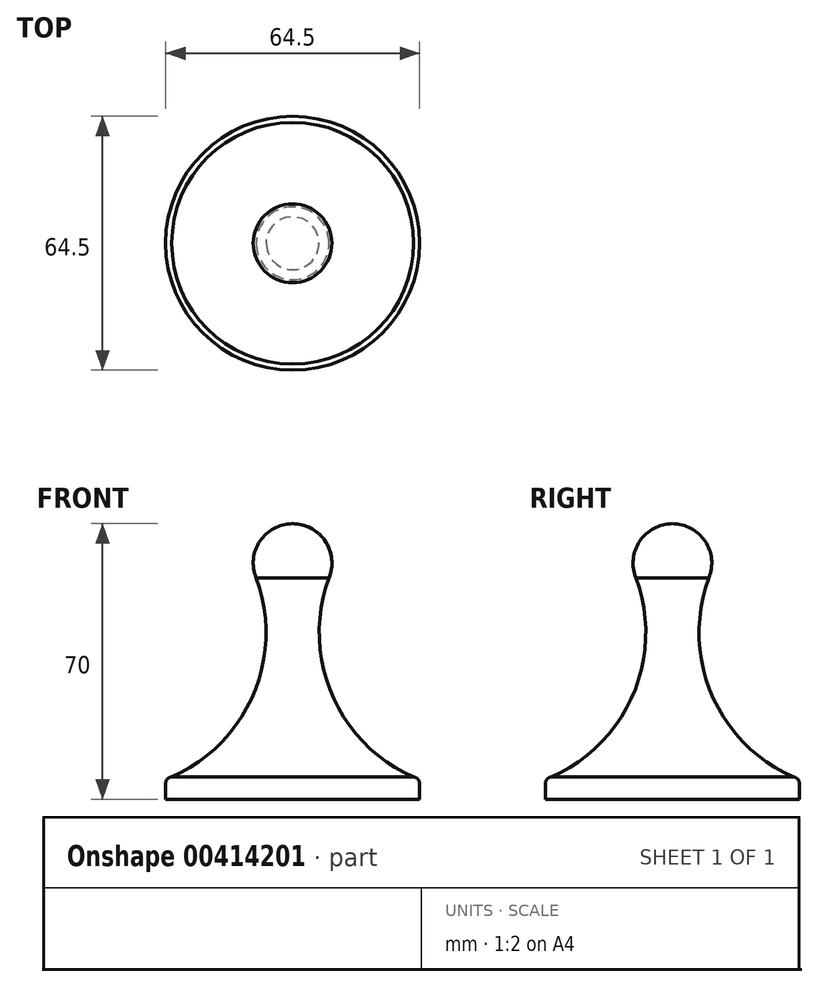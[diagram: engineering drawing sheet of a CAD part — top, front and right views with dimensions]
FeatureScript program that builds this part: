
annotation { "Feature Type Name" : "Feature", "Feature Type Description" : "" }
export const myFeature = defineFeature(function(context is Context, id is Id, definition is map)
    precondition{}
    {
        {
            var Q0;
            Q0=qCreatedBy(makeId("Front.planeOp"),FACE);
            var sketch = newSketch(context, id + "F0", { "sketchPlane" : qUnion([Q0])});
            skLineSegment(sketch, "E0", {"start": v(0, 0) * mm, "end": v(0, 60) * mm});
            skLineSegment(sketch, "E1", {"start": v(0, 0) * mm, "end": v(32.25, 0) * mm});
            skLineSegment(sketch, "E2", {"start": v(32.25, 0) * mm, "end": v(32.25, 4) * mm});
            skArc(sketch, "E3", {"start": v(32.25, 4) * mm, "mid": v(31.8, 5.14) * mm, "end": v(30.7, 5.67) * mm});
            skLineSegment(sketch, "E4", {"start": v(0, 60) * mm, "end": v(0, 70) * mm});
            skArc(sketch, "E5.trimOffspring", {"start": v(9.26, 56.21) * mm, "mid": v(8.3, 65.57) * mm, "end": v(0, 70) * mm});
            skArc(sketch, "E6", {"start": v(9.26, 56.21) * mm, "mid": v(9.94, 26.68) * mm, "end": v(30.7, 5.67) * mm});
            skSolve(sketch);
        }
        {
            var Q0;
            Q0=makeQuery(id+"F0.imprint","IMPRINT",FACE,{"disambiguationData":[TD([[makeQuery(id+"F0.imprint","IMPRINT",EDGE,{"derivedFrom":sQuery(id+"F0.wireOp",EDGE,"E0")}),-1.0]])]});
            var Q1;
            Q1=sQuery(id+"F0.wireOp",EDGE,"E0");
            revolve(context, id + "F1", {"entities" : qUnion([Q0]), "axis" : qUnion([Q1]), "revolveType" : RevolveType.FULL});
        }
    });
